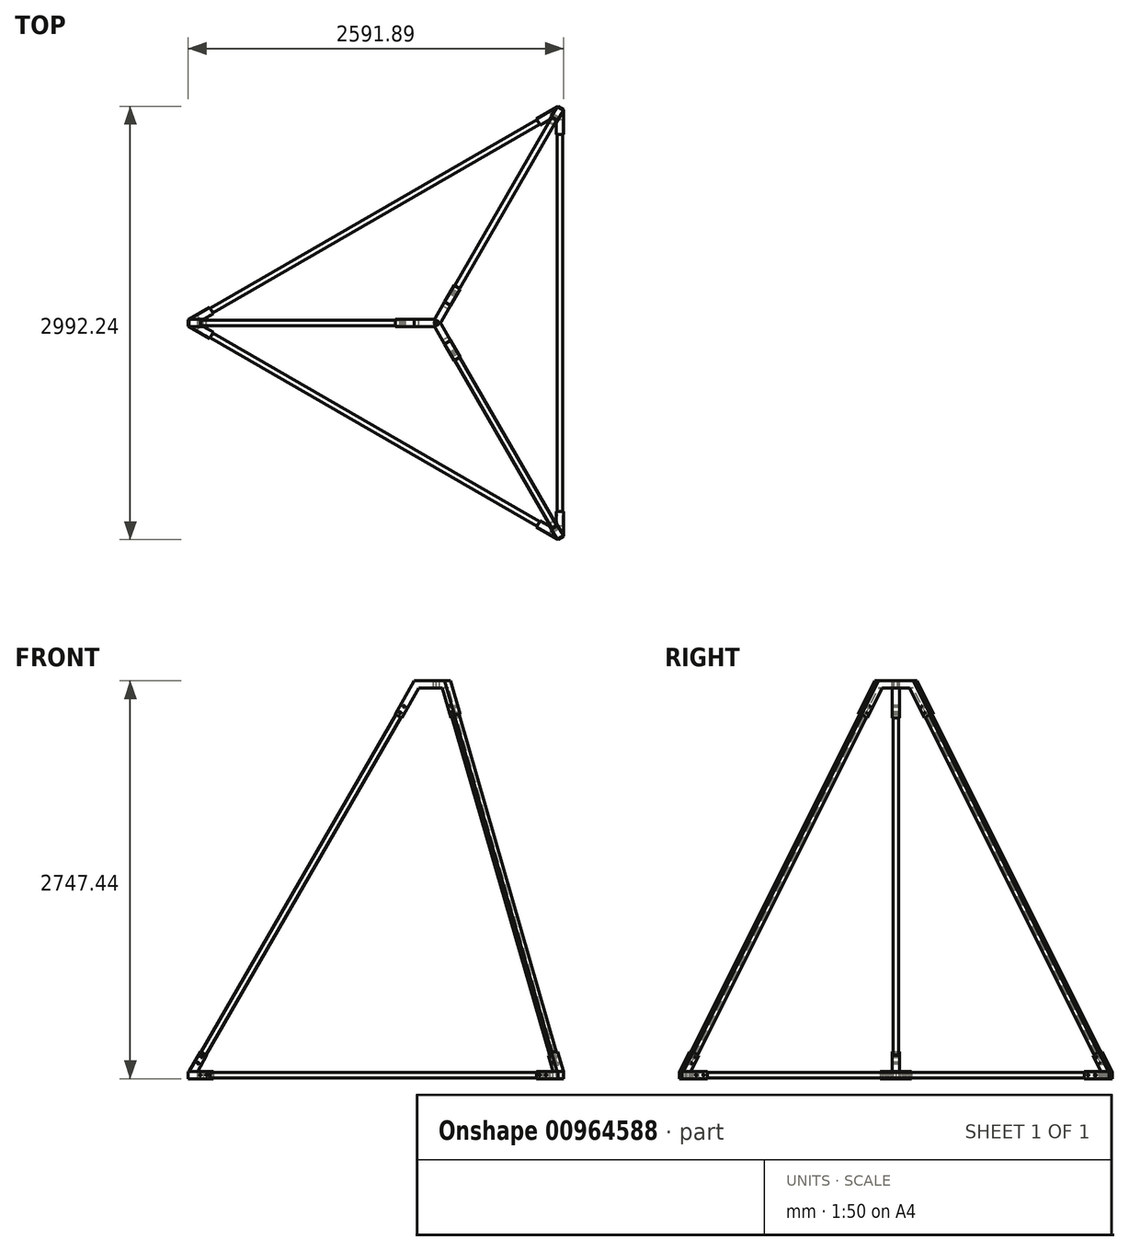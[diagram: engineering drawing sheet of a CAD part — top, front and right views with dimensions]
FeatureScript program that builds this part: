
annotation { "Feature Type Name" : "Feature", "Feature Type Description" : "" }
export const myFeature = defineFeature(function(context is Context, id is Id, definition is map)
    precondition{}
    {
        {
            var Q0;
            Q0=qCreatedBy(makeId("Top.planeOp"),FACE);
            var sketch = newSketch(context, id + "F0", { "sketchPlane" : qUnion([Q0])});
            skLineSegment(sketch, "E0", {"start": v(0, 0) * mm, "end": v(-1651, 0) * mm, "construction": true});
            skLineSegment(sketch, "E1", {"start": v(-1651, 0) * mm, "end": v(-1541.01, 63.5) * mm});
            skLineSegment(sketch, "E2", {"start": v(-1541.01, 63.5) * mm, "end": v(-1566.41, 107.5) * mm});
            skLineSegment(sketch, "E3", {"start": v(-1651, 0) * mm, "end": v(-1541.01, -63.5) * mm});
            skLineSegment(sketch, "E4", {"start": v(-1541.01, -63.5) * mm, "end": v(-1566.41, -107.5) * mm});
            skLineSegment(sketch, "E5", {"start": v(-1566.41, 107.5) * mm, "end": v(-1715.06, 21.67) * mm});
            skLineSegment(sketch, "E6", {"start": v(-1566.41, -107.5) * mm, "end": v(-1715.06, -21.67) * mm});
            skLineSegment(sketch, "E7", {"start": v(-1715.06, -21.67) * mm, "end": v(-1715.06, 21.67) * mm});
            skSolve(sketch);
        }
        {
            var Q0;
            Q0 = qSketchRegion(id + "F0", true);
            extrude(context, id + "F1", {"entities" : qUnion([Q0]), "depth" : 50.8 * mm, "offsetDistance" : 25.4 * mm});
        }
        {
            var Q0;
            Q0=makeQuery(id+"F1.opExtrude","CAP_FACE",FACE,{"disambiguationData":[OSD([sQuery(id+"F0.wireOp",EDGE,"E1"),sQuery(id+"F0.wireOp",EDGE,"E2"),sQuery(id+"F0.wireOp",EDGE,"E3"),sQuery(id+"F0.wireOp",EDGE,"E4"),sQuery(id+"F0.wireOp",EDGE,"E5"),sQuery(id+"F0.wireOp",EDGE,"E6"),sQuery(id+"F0.wireOp",EDGE,"E7")])],"isStart":false});
            var sketch = newSketch(context, id + "F2", { "sketchPlane" : qUnion([Q0])});
            skLineSegment(sketch, "E8", {"start": v(-1651, 58.66) * mm, "end": v(-1651, -58.66) * mm, "construction": true});
            skSolve(sketch);
        }
        {
            var Q0;
            Q0=sQuery(id+"F2.wireOp",EDGE,"E8");
            cPlane(context, id + "F3", {"entities" : qUnion([Q0]), "cplaneType" : CPlaneType.MID_PLANE, "offset" : 25.4 * mm, "width" : 152.4 * mm, "height" : 152.4 * mm});
        }
        {
            var Q0;
            Q0=qCreatedBy(id+"F3.planeOp",FACE);
            var sketch = newSketch(context, id + "F4", { "sketchPlane" : qUnion([Q0])});
            skLineSegment(sketch, "E9", {"start": v(-1587.5, 160.79) * mm, "end": v(-1651, 50.8) * mm});
            skLineSegment(sketch, "E10", {"start": v(-1587.5, 160.79) * mm, "end": v(-1631.5, 186.19) * mm});
            skLineSegment(sketch, "E11", {"start": v(-1631.5, 186.19) * mm, "end": v(-1709.66, 50.8) * mm});
            skLineSegment(sketch, "E12", {"start": v(-1709.66, 50.8) * mm, "end": v(-1651, 50.8) * mm});
            skSolve(sketch);
        }
        {
            var Q0;
            Q0 = qSketchRegion(id + "F4", true);
            extrude(context, id + "F5", {"entities" : qUnion([Q0]), "operationType" : NewBodyOperationType.ADD, "endBound" : BoundingType.SYMMETRIC, "depth" : 50.8 * mm, "offsetDistance" : 25.4 * mm});
        }
        {
            var Q0;
            Q0=qCreatedBy(makeId("Right.planeOp"),FACE);
            var sketch = newSketch(context, id + "F6", { "sketchPlane" : qUnion([Q0])});
            skLineSegment(sketch, "E13", {"start": v(0, 38.57) * mm, "end": v(0, -54.11) * mm, "construction": true});
            skSolve(sketch);
        }
        {
            var Q0;
            Q0=makeQuery(id+"F1.opExtrude","SWEPT_FACE",FACE,{"disambiguationData":[OSD([sQuery(id+"F0.wireOp",EDGE,"E4")])]});
            var sketch = newSketch(context, id + "F7", { "sketchPlane" : qUnion([Q0])});
            skLineSegment(sketch, "E14.bottom", {"start": v(-869.95, 44.45) * mm, "end": v(-831.85, 44.45) * mm});
            skLineSegment(sketch, "E14.top", {"start": v(-869.95, 6.35) * mm, "end": v(-831.85, 6.35) * mm});
            skLineSegment(sketch, "E14.left", {"start": v(-869.95, 44.45) * mm, "end": v(-869.95, 6.35) * mm});
            skLineSegment(sketch, "E14.right", {"start": v(-831.85, 44.45) * mm, "end": v(-831.85, 6.35) * mm});
            skSolve(sketch);
        }
        {
            var Q0;
            Q0=makeQuery(id+"F1.opExtrude","SWEPT_FACE",FACE,{"disambiguationData":[OSD([sQuery(id+"F0.wireOp",EDGE,"E2")])]});
            var sketch = newSketch(context, id + "F8", { "sketchPlane" : qUnion([Q0])});
            skLineSegment(sketch, "E15.bottom", {"start": v(869.95, 44.45) * mm, "end": v(831.85, 44.45) * mm});
            skLineSegment(sketch, "E15.top", {"start": v(869.95, 6.35) * mm, "end": v(831.85, 6.35) * mm});
            skLineSegment(sketch, "E15.left", {"start": v(869.95, 44.45) * mm, "end": v(869.95, 6.35) * mm});
            skLineSegment(sketch, "E15.right", {"start": v(831.85, 44.45) * mm, "end": v(831.85, 6.35) * mm});
            skSolve(sketch);
        }
        {
            var Q0;
            Q0=makeQuery(id+"F5.opExtrude","SWEPT_FACE",FACE,{"disambiguationData":[OSD([sQuery(id+"F4.wireOp",EDGE,"E10")])]});
            var sketch = newSketch(context, id + "F9", { "sketchPlane" : qUnion([Q0])});
            skLineSegment(sketch, "E16.bottom", {"start": v(-1499.66, -19.05) * mm, "end": v(-1461.56, -19.05) * mm});
            skLineSegment(sketch, "E16.top", {"start": v(-1499.66, 19.05) * mm, "end": v(-1461.56, 19.05) * mm});
            skLineSegment(sketch, "E16.left", {"start": v(-1499.66, -19.05) * mm, "end": v(-1499.66, 19.05) * mm});
            skLineSegment(sketch, "E16.right", {"start": v(-1461.56, -19.05) * mm, "end": v(-1461.56, 19.05) * mm});
            skSolve(sketch);
        }
        {
            var Q0;
            Q0 = qSketchRegion(id + "F7", true);
            extrude(context, id + "F10", {"entities" : qUnion([Q0]), "operationType" : NewBodyOperationType.REMOVE, "oppositeDirection" : true, "depth" : 101.6 * mm, "offsetDistance" : 25.4 * mm});
        }
        {
            var Q0;
            Q0 = qSketchRegion(id + "F8", true);
            extrude(context, id + "F11", {"entities" : qUnion([Q0]), "operationType" : NewBodyOperationType.REMOVE, "oppositeDirection" : true, "depth" : 101.6 * mm, "offsetDistance" : 25.4 * mm});
        }
        {
            var Q0;
            Q0 = qSketchRegion(id + "F9", true);
            extrude(context, id + "F12", {"entities" : qUnion([Q0]), "operationType" : NewBodyOperationType.REMOVE, "oppositeDirection" : true, "depth" : 101.6 * mm, "offsetDistance" : 25.4 * mm});
        }
        {
            var Q0;
            Q0=makeQuery(id+"F5.opExtrude","SWEPT_FACE",FACE,{"disambiguationData":[OSD([sQuery(id+"F4.wireOp",EDGE,"E10")])]});
            var sketch = newSketch(context, id + "F13", { "sketchPlane" : qUnion([Q0])});
            skLineSegment(sketch, "E17.bottom", {"start": v(-1499.66, -19.05) * mm, "end": v(-1461.56, -19.05) * mm});
            skLineSegment(sketch, "E17.top", {"start": v(-1499.66, 19.05) * mm, "end": v(-1461.56, 19.05) * mm});
            skLineSegment(sketch, "E17.left", {"start": v(-1499.66, -19.05) * mm, "end": v(-1499.66, 19.05) * mm});
            skLineSegment(sketch, "E17.right", {"start": v(-1461.56, -19.05) * mm, "end": v(-1461.56, 19.05) * mm});
            skSolve(sketch);
        }
        {
            var Q0;
            Q0 = qSketchRegion(id + "F13", true);
            extrude(context, id + "F14", {"entities" : qUnion([Q0]), "oppositeDirection" : true, "depth" : 101.6 * mm, "offsetDistance" : 25.4 * mm});
        }
        {
            var Q0;
            Q0=makeQuery(id+"F14.opExtrude","CAP_FACE",FACE,{"disambiguationData":[OSD([sQuery(id+"F13.wireOp",EDGE,"E17.bottom"),sQuery(id+"F13.wireOp",EDGE,"E17.top"),sQuery(id+"F13.wireOp",EDGE,"E17.left"),sQuery(id+"F13.wireOp",EDGE,"E17.right")])],"isStart":true});
            extrude(context, id + "F15", {"entities" : qUnion([Q0]), "operationType" : NewBodyOperationType.ADD, "depth" : 2794 * mm, "offsetDistance" : 25.4 * mm});
        }
        {
            var Q0;
            Q0=qCreatedBy(id+"F3.planeOp",FACE);
            var sketch = newSketch(context, id + "F16", { "sketchPlane" : qUnion([Q0])});
            skLineSegment(sketch, "E18", {"start": v(-279.8, 2514.7) * mm, "end": v(-285.3, 2517.87) * mm});
            skLineSegment(sketch, "E19", {"start": v(-285.3, 2517.87) * mm, "end": v(-152.75, 2747.44) * mm});
            skLineSegment(sketch, "E20", {"start": v(-246.8, 2495.65) * mm, "end": v(-241.3, 2492.47) * mm});
            skLineSegment(sketch, "E21", {"start": v(-241.3, 2492.47) * mm, "end": v(-123.42, 2696.64) * mm});
            skLineSegment(sketch, "E22", {"start": v(-123.42, 2696.64) * mm, "end": v(0, 2696.64) * mm});
            skLineSegment(sketch, "E23", {"start": v(0, 2696.64) * mm, "end": v(0, 2747.44) * mm});
            skLineSegment(sketch, "E24", {"start": v(-152.75, 2747.44) * mm, "end": v(0, 2747.44) * mm});
            skLineSegment(sketch, "E25", {"start": v(-246.8, 2495.65) * mm, "end": v(-196, 2583.64) * mm});
            skLineSegment(sketch, "E26", {"start": v(-279.8, 2514.7) * mm, "end": v(-229, 2602.69) * mm});
            skLineSegment(sketch, "E27", {"start": v(-229, 2602.69) * mm, "end": v(-196, 2583.64) * mm});
            skSolve(sketch);
        }
        {
            var Q0;
            Q0 = qSketchRegion(id + "F16", true);
            extrude(context, id + "F17", {"entities" : qUnion([Q0]), "endBound" : BoundingType.SYMMETRIC, "depth" : 50.8 * mm, "offsetDistance" : 25.4 * mm});
        }
        {
            var Q0;
            Q0=makeQuery(id+"F17.opExtrude","CAP_FACE",FACE,{"disambiguationData":[OSD([sQuery(id+"F16.wireOp",EDGE,"E18"),sQuery(id+"F16.wireOp",EDGE,"E19"),sQuery(id+"F16.wireOp",EDGE,"E20"),sQuery(id+"F16.wireOp",EDGE,"E21"),sQuery(id+"F16.wireOp",EDGE,"E22"),sQuery(id+"F16.wireOp",EDGE,"E23"),sQuery(id+"F16.wireOp",EDGE,"E24"),sQuery(id+"F16.wireOp",EDGE,"E25"),sQuery(id+"F16.wireOp",EDGE,"E26"),sQuery(id+"F16.wireOp",EDGE,"E27")])],"isStart":false});
            var sketch = newSketch(context, id + "F18", { "sketchPlane" : qUnion([Q0])});
            skLineSegment(sketch, "E28", {"start": v(-229, 2602.69) * mm, "end": v(-196, 2583.64) * mm});
            skLineSegment(sketch, "E29", {"start": v(-196, 2583.64) * mm, "end": v(-246.8, 2495.65) * mm});
            skLineSegment(sketch, "E30", {"start": v(-246.8, 2495.65) * mm, "end": v(-279.8, 2514.7) * mm});
            skLineSegment(sketch, "E31", {"start": v(-279.8, 2514.7) * mm, "end": v(-229, 2602.69) * mm});
            skSolve(sketch);
        }
        {
            var Q0;
            Q0=makeQuery(id+"F17.opExtrude","CAP_FACE",FACE,{"disambiguationData":[OSD([sQuery(id+"F16.wireOp",EDGE,"E18"),sQuery(id+"F16.wireOp",EDGE,"E19"),sQuery(id+"F16.wireOp",EDGE,"E20"),sQuery(id+"F16.wireOp",EDGE,"E21"),sQuery(id+"F16.wireOp",EDGE,"E22"),sQuery(id+"F16.wireOp",EDGE,"E23"),sQuery(id+"F16.wireOp",EDGE,"E24"),sQuery(id+"F16.wireOp",EDGE,"E25"),sQuery(id+"F16.wireOp",EDGE,"E26"),sQuery(id+"F16.wireOp",EDGE,"E27")])],"isStart":true});
            var sketch = newSketch(context, id + "F19", { "sketchPlane" : qUnion([Q0])});
            skLineSegment(sketch, "E32", {"start": v(229, 2602.69) * mm, "end": v(279.8, 2514.7) * mm});
            skLineSegment(sketch, "E33", {"start": v(279.8, 2514.7) * mm, "end": v(246.8, 2495.65) * mm});
            skLineSegment(sketch, "E34", {"start": v(246.8, 2495.65) * mm, "end": v(196, 2583.64) * mm});
            skLineSegment(sketch, "E35", {"start": v(196, 2583.64) * mm, "end": v(229, 2602.69) * mm});
            skSolve(sketch);
        }
        {
            var Q0;
            Q0 = qSketchRegion(id + "F18", true);
            extrude(context, id + "F20", {"entities" : qUnion([Q0]), "operationType" : NewBodyOperationType.ADD, "oppositeDirection" : true, "depth" : 6.35 * mm, "offsetDistance" : 25.4 * mm});
        }
        {
            var Q0;
            Q0 = qSketchRegion(id + "F19", true);
            extrude(context, id + "F21", {"entities" : qUnion([Q0]), "operationType" : NewBodyOperationType.ADD, "oppositeDirection" : true, "depth" : 6.35 * mm, "offsetDistance" : 25.4 * mm});
        }
        {
            var Q0;
            Q0=makeQuery(id+"F5.opExtrude","CAP_FACE",FACE,{"disambiguationData":[OSD([sQuery(id+"F4.wireOp",EDGE,"E9"),sQuery(id+"F4.wireOp",EDGE,"E10"),sQuery(id+"F4.wireOp",EDGE,"E11"),sQuery(id+"F4.wireOp",EDGE,"E12")])],"isStart":false});
            var sketch = newSketch(context, id + "F22", { "sketchPlane" : qUnion([Q0])});
            skLineSegment(sketch, "E36", {"start": v(-1609.5, 173.49) * mm, "end": v(-1647.6, 107.5) * mm, "construction": true});
            skCircle(sketch, "E37", {"center": v(-1622.2, 151.49) * mm, "radius": 6.35 * mm});
            skCircle(sketch, "E38", {"center": v(-1647.6, 107.5) * mm, "radius": 6.35 * mm});
            skSolve(sketch);
        }
        {
            var Q0;
            Q0=makeQuery(id+"F1.opExtrude","SWEPT_FACE",FACE,{"disambiguationData":[OSD([sQuery(id+"F0.wireOp",EDGE,"E6")])]});
            var sketch = newSketch(context, id + "F23", { "sketchPlane" : qUnion([Q0])});
            skLineSegment(sketch, "E39", {"start": v(-1302.8, 25.4) * mm, "end": v(-1379, 25.4) * mm, "construction": true});
            skCircle(sketch, "E40", {"center": v(-1328.2, 25.4) * mm, "radius": 6.35 * mm});
            skCircle(sketch, "E41", {"center": v(-1379, 25.4) * mm, "radius": 6.35 * mm});
            skSolve(sketch);
        }
        {
            var Q0;
            Q0=makeQuery(id+"F1.opExtrude","SWEPT_FACE",FACE,{"disambiguationData":[OSD([sQuery(id+"F0.wireOp",EDGE,"E5")])]});
            var sketch = newSketch(context, id + "F24", { "sketchPlane" : qUnion([Q0])});
            skLineSegment(sketch, "E42", {"start": v(1302.8, 25.4) * mm, "end": v(1379, 25.4) * mm, "construction": true});
            skCircle(sketch, "E43", {"center": v(1328.2, 25.4) * mm, "radius": 6.35 * mm});
            skCircle(sketch, "E44", {"center": v(1379, 25.4) * mm, "radius": 6.35 * mm});
            skSolve(sketch);
        }
        {
            var Q0;
            Q0=makeQuery(id+"F20.boolean.opBoolean","MERGE",FACE,{"derivedFrom":[makeQuery(id+"F17.opExtrude","CAP_FACE",FACE,{"disambiguationData":[OSD([sQuery(id+"F16.wireOp",EDGE,"E18"),sQuery(id+"F16.wireOp",EDGE,"E19"),sQuery(id+"F16.wireOp",EDGE,"E20"),sQuery(id+"F16.wireOp",EDGE,"E21"),sQuery(id+"F16.wireOp",EDGE,"E22"),sQuery(id+"F16.wireOp",EDGE,"E23"),sQuery(id+"F16.wireOp",EDGE,"E24"),sQuery(id+"F16.wireOp",EDGE,"E25"),sQuery(id+"F16.wireOp",EDGE,"E26"),sQuery(id+"F16.wireOp",EDGE,"E27")])],"isStart":false}),makeQuery(id+"F20.opExtrude","CAP_FACE",FACE,{"disambiguationData":[OSD([sQuery(id+"F18.wireOp",EDGE,"E28"),sQuery(id+"F18.wireOp",EDGE,"E29"),sQuery(id+"F18.wireOp",EDGE,"E30"),sQuery(id+"F18.wireOp",EDGE,"E31")])],"isStart":true})]});
            var sketch = newSketch(context, id + "F25", { "sketchPlane" : qUnion([Q0])});
            skLineSegment(sketch, "E45", {"start": v(-1128.45, 1006.68) * mm, "end": v(-263.3, 2505.17) * mm, "construction": true});
            skCircle(sketch, "E46", {"center": v(-250.6, 2527.17) * mm, "radius": 6.35 * mm});
            skCircle(sketch, "E47", {"center": v(-225.2, 2571.16) * mm, "radius": 6.35 * mm});
            skSolve(sketch);
        }
        {
            var Q0;
            Q0 = qSketchRegion(id + "F22", true);
            var Q1;
            Q1=makeQuery(id+"F5.opExtrude","CAP_FACE",FACE,{"disambiguationData":[OSD([sQuery(id+"F4.wireOp",EDGE,"E9"),sQuery(id+"F4.wireOp",EDGE,"E10"),sQuery(id+"F4.wireOp",EDGE,"E11"),sQuery(id+"F4.wireOp",EDGE,"E12")])],"isStart":true});
            extrude(context, id + "F26", {"entities" : qUnion([Q0]), "operationType" : NewBodyOperationType.REMOVE, "endBound" : BoundingType.UP_TO_SURFACE, "oppositeDirection" : true, "depth" : 25.4 * mm, "endBoundEntityFace" : qUnion([Q1]), "offsetDistance" : 25.4 * mm});
        }
        {
            var Q0;
            Q0 = qSketchRegion(id + "F23", true);
            var Q1;
            Q1=makeQuery(id+"F1.opExtrude","SWEPT_FACE",FACE,{"disambiguationData":[OSD([sQuery(id+"F0.wireOp",EDGE,"E3")])]});
            extrude(context, id + "F27", {"entities" : qUnion([Q0]), "operationType" : NewBodyOperationType.REMOVE, "endBound" : BoundingType.UP_TO_SURFACE, "oppositeDirection" : true, "depth" : 25.4 * mm, "endBoundEntityFace" : qUnion([Q1]), "offsetDistance" : 25.4 * mm});
        }
        {
            var Q0;
            Q0 = qSketchRegion(id + "F24", true);
            var Q1;
            Q1=makeQuery(id+"F1.opExtrude","SWEPT_FACE",FACE,{"disambiguationData":[OSD([sQuery(id+"F0.wireOp",EDGE,"E1")])]});
            extrude(context, id + "F28", {"entities" : qUnion([Q0]), "operationType" : NewBodyOperationType.REMOVE, "endBound" : BoundingType.UP_TO_SURFACE, "oppositeDirection" : true, "depth" : 25.4 * mm, "endBoundEntityFace" : qUnion([Q1]), "offsetDistance" : 25.4 * mm});
        }
        {
            var Q0;
            Q0 = qSketchRegion(id + "F25", true);
            var Q1;
            Q1=makeQuery(id+"F21.boolean.opBoolean","MERGE",FACE,{"derivedFrom":[makeQuery(id+"F17.opExtrude","CAP_FACE",FACE,{"disambiguationData":[OSD([sQuery(id+"F16.wireOp",EDGE,"E18"),sQuery(id+"F16.wireOp",EDGE,"E19"),sQuery(id+"F16.wireOp",EDGE,"E20"),sQuery(id+"F16.wireOp",EDGE,"E21"),sQuery(id+"F16.wireOp",EDGE,"E22"),sQuery(id+"F16.wireOp",EDGE,"E23"),sQuery(id+"F16.wireOp",EDGE,"E24"),sQuery(id+"F16.wireOp",EDGE,"E25"),sQuery(id+"F16.wireOp",EDGE,"E26"),sQuery(id+"F16.wireOp",EDGE,"E27")])],"isStart":true}),makeQuery(id+"F21.opExtrude","CAP_FACE",FACE,{"disambiguationData":[OSD([sQuery(id+"F19.wireOp",EDGE,"E32"),sQuery(id+"F19.wireOp",EDGE,"E33"),sQuery(id+"F19.wireOp",EDGE,"E34"),sQuery(id+"F19.wireOp",EDGE,"E35")])],"isStart":true})]});
            extrude(context, id + "F29", {"entities" : qUnion([Q0]), "operationType" : NewBodyOperationType.REMOVE, "endBound" : BoundingType.UP_TO_SURFACE, "oppositeDirection" : true, "depth" : 25.4 * mm, "endBoundEntityFace" : qUnion([Q1]), "offsetDistance" : 25.4 * mm});
        }
        {
            var Q0;
            Q0=makeQuery(id+"F1.opExtrude","SWEPT_BODY",BODY,{"disambiguationData":[OSD([sQuery(id+"F0.wireOp",EDGE,"E1"),sQuery(id+"F0.wireOp",EDGE,"E2"),sQuery(id+"F0.wireOp",EDGE,"E3"),sQuery(id+"F0.wireOp",EDGE,"E4"),sQuery(id+"F0.wireOp",EDGE,"E5"),sQuery(id+"F0.wireOp",EDGE,"E6"),sQuery(id+"F0.wireOp",EDGE,"E7")])]});
            var Q1;
            Q1=makeQuery(id+"F14.opExtrude","SWEPT_BODY",BODY,{"disambiguationData":[OSD([sQuery(id+"F13.wireOp",EDGE,"E17.bottom"),sQuery(id+"F13.wireOp",EDGE,"E17.top"),sQuery(id+"F13.wireOp",EDGE,"E17.left"),sQuery(id+"F13.wireOp",EDGE,"E17.right")])]});
            var Q2;
            Q2=makeQuery(id+"F17.opExtrude","SWEPT_BODY",BODY,{"disambiguationData":[OSD([sQuery(id+"F16.wireOp",EDGE,"E18"),sQuery(id+"F16.wireOp",EDGE,"E19"),sQuery(id+"F16.wireOp",EDGE,"E20"),sQuery(id+"F16.wireOp",EDGE,"E21"),sQuery(id+"F16.wireOp",EDGE,"E22"),sQuery(id+"F16.wireOp",EDGE,"E23"),sQuery(id+"F16.wireOp",EDGE,"E24"),sQuery(id+"F16.wireOp",EDGE,"E25"),sQuery(id+"F16.wireOp",EDGE,"E26"),sQuery(id+"F16.wireOp",EDGE,"E27")])]});
            var Q3;
            Q3=sQuery(id+"F6.wireOp",EDGE,"E13");
            circularPattern(context, id + "F30", {"entities" : qUnion([Q0, Q1, Q2]), "axis" : qUnion([Q3]), "angle" : 360 * degree, "instanceCount" : 3, "equalSpace" : true});
        }
        {
            var Q0;
            Q0=makeQuery(id+"F1.opExtrude","SWEPT_FACE",FACE,{"disambiguationData":[OSD([sQuery(id+"F0.wireOp",EDGE,"E4")])]});
            var sketch = newSketch(context, id + "F31", { "sketchPlane" : qUnion([Q0])});
            skLineSegment(sketch, "E48.bottom", {"start": v(-831.85, 44.45) * mm, "end": v(-869.95, 44.45) * mm});
            skLineSegment(sketch, "E48.top", {"start": v(-831.85, 6.35) * mm, "end": v(-869.95, 6.35) * mm});
            skLineSegment(sketch, "E48.left", {"start": v(-831.85, 44.45) * mm, "end": v(-831.85, 6.35) * mm});
            skLineSegment(sketch, "E48.right", {"start": v(-869.95, 44.45) * mm, "end": v(-869.95, 6.35) * mm});
            skSolve(sketch);
        }
        {
            var Q0;
            Q0 = qSketchRegion(id + "F31", true);
            var Q1;
            Q1=makeQuery(id+"F30.opPattern","COPY",FACE,{"derivedFrom":makeQuery(id+"F11.boolean.opBoolean","COPY",FACE,{"derivedFrom":makeQuery(id+"F11.opExtrude","CAP_FACE",FACE,{"disambiguationData":[OSD([sQuery(id+"F8.wireOp",EDGE,"E15.bottom"),sQuery(id+"F8.wireOp",EDGE,"E15.top"),sQuery(id+"F8.wireOp",EDGE,"E15.left"),sQuery(id+"F8.wireOp",EDGE,"E15.right")])],"isStart":false})}),"instanceName":"2"});
            extrude(context, id + "F32", {"entities" : qUnion([Q0]), "oppositeDirection" : true, "depth" : 101.6 * mm, "offsetDistance" : 25.4 * mm, "hasSecondDirection" : true, "secondDirectionBound" : SecondDirectionBoundingType.UP_TO_SURFACE, "secondDirectionOppositeDirection" : false, "secondDirectionDepth" : 1524 * mm, "secondDirectionBoundEntityFace" : qUnion([Q1])});
        }
        {
            var Q0;
            Q0=makeQuery(id+"F1.opExtrude","SWEPT_FACE",FACE,{"disambiguationData":[OSD([sQuery(id+"F0.wireOp",EDGE,"E2")])]});
            var sketch = newSketch(context, id + "F33", { "sketchPlane" : qUnion([Q0])});
            skLineSegment(sketch, "E49.bottom", {"start": v(869.95, 44.45) * mm, "end": v(831.85, 44.45) * mm});
            skLineSegment(sketch, "E49.top", {"start": v(869.95, 6.35) * mm, "end": v(831.85, 6.35) * mm});
            skLineSegment(sketch, "E49.left", {"start": v(869.95, 44.45) * mm, "end": v(869.95, 6.35) * mm});
            skLineSegment(sketch, "E49.right", {"start": v(831.85, 44.45) * mm, "end": v(831.85, 6.35) * mm});
            skSolve(sketch);
        }
        {
            var Q0;
            Q0 = qSketchRegion(id + "F33", true);
            var Q1;
            Q1=makeQuery(id+"F30.opPattern","COPY",FACE,{"derivedFrom":makeQuery(id+"F10.boolean.opBoolean","COPY",FACE,{"derivedFrom":makeQuery(id+"F10.opExtrude","CAP_FACE",FACE,{"disambiguationData":[OSD([sQuery(id+"F7.wireOp",EDGE,"E14.bottom"),sQuery(id+"F7.wireOp",EDGE,"E14.top"),sQuery(id+"F7.wireOp",EDGE,"E14.left"),sQuery(id+"F7.wireOp",EDGE,"E14.right")])],"isStart":false})}),"instanceName":"1"});
            extrude(context, id + "F34", {"entities" : qUnion([Q0]), "oppositeDirection" : true, "depth" : 101.6 * mm, "offsetDistance" : 25.4 * mm, "hasSecondDirection" : true, "secondDirectionBound" : SecondDirectionBoundingType.UP_TO_SURFACE, "secondDirectionOppositeDirection" : false, "secondDirectionDepth" : 25.4 * mm, "secondDirectionBoundEntityFace" : qUnion([Q1])});
        }
        {
            var Q0;
            Q0=makeQuery(id+"F30.opPattern","COPY",FACE,{"derivedFrom":makeQuery(id+"F1.opExtrude","SWEPT_FACE",FACE,{"disambiguationData":[OSD([sQuery(id+"F0.wireOp",EDGE,"E4")])]}),"instanceName":"2"});
            var sketch = newSketch(context, id + "F35", { "sketchPlane" : qUnion([Q0])});
            skLineSegment(sketch, "E50.bottom", {"start": v(-831.85, 44.45) * mm, "end": v(-869.95, 44.45) * mm});
            skLineSegment(sketch, "E50.top", {"start": v(-831.85, 6.35) * mm, "end": v(-869.95, 6.35) * mm});
            skLineSegment(sketch, "E50.left", {"start": v(-831.85, 44.45) * mm, "end": v(-831.85, 6.35) * mm});
            skLineSegment(sketch, "E50.right", {"start": v(-869.95, 44.45) * mm, "end": v(-869.95, 6.35) * mm});
            skSolve(sketch);
        }
        {
            var Q0;
            Q0 = qSketchRegion(id + "F35", true);
            var Q1;
            Q1=makeQuery(id+"F30.opPattern","COPY",FACE,{"derivedFrom":makeQuery(id+"F11.boolean.opBoolean","COPY",FACE,{"derivedFrom":makeQuery(id+"F11.opExtrude","CAP_FACE",FACE,{"disambiguationData":[OSD([sQuery(id+"F8.wireOp",EDGE,"E15.bottom"),sQuery(id+"F8.wireOp",EDGE,"E15.top"),sQuery(id+"F8.wireOp",EDGE,"E15.left"),sQuery(id+"F8.wireOp",EDGE,"E15.right")])],"isStart":false})}),"instanceName":"1"});
            extrude(context, id + "F36", {"entities" : qUnion([Q0]), "oppositeDirection" : true, "depth" : 101.6 * mm, "offsetDistance" : 25.4 * mm, "hasSecondDirection" : true, "secondDirectionBound" : SecondDirectionBoundingType.UP_TO_SURFACE, "secondDirectionOppositeDirection" : false, "secondDirectionDepth" : 25.4 * mm, "secondDirectionBoundEntityFace" : qUnion([Q1])});
        }
    });
